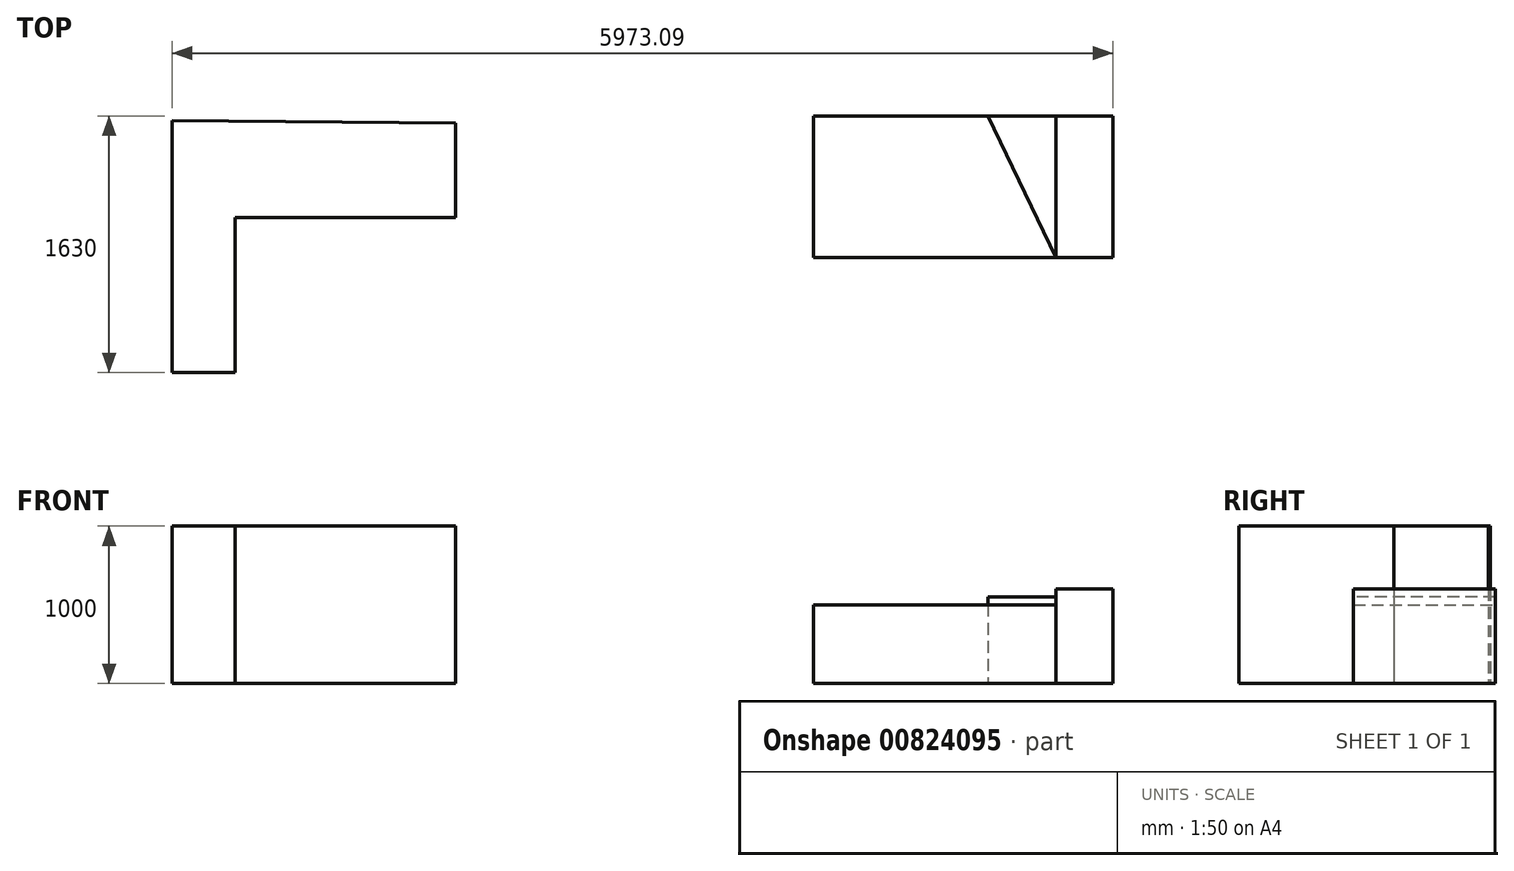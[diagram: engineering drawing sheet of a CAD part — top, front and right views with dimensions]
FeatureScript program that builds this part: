
annotation { "Feature Type Name" : "Feature", "Feature Type Description" : "" }
export const myFeature = defineFeature(function(context is Context, id is Id, definition is map)
    precondition{}
    {
        {
            var Q0;
            Q0=qCreatedBy(makeId("Top.planeOp"),FACE);
            var sketch = newSketch(context, id + "F0", { "sketchPlane" : qUnion([Q0])});
            skLineSegment(sketch, "E0.bottom", {"start": v(-91.66, 3961.41) * mm, "end": v(5908.34, 3961.41) * mm});
            skLineSegment(sketch, "E0.top", {"start": v(-91.66, -38.59) * mm, "end": v(5908.34, -38.59) * mm});
            skLineSegment(sketch, "E0.left", {"start": v(-91.66, 3961.41) * mm, "end": v(-91.66, -38.59) * mm});
            skLineSegment(sketch, "E0.right", {"start": v(5908.34, 3961.41) * mm, "end": v(5908.34, -38.59) * mm});
            skLineSegment(sketch, "E1", {"start": v(-91.66, 3926.3) * mm, "end": v(-91.66, 2326.3) * mm});
            skLineSegment(sketch, "E2", {"start": v(-91.66, 2326.3) * mm, "end": v(308.34, 2326.3) * mm});
            skLineSegment(sketch, "E3", {"start": v(308.34, 2326.3) * mm, "end": v(308.34, 3310.65) * mm});
            skLineSegment(sketch, "E4", {"start": v(308.34, 3310.65) * mm, "end": v(1708.27, 3310.65) * mm});
            skLineSegment(sketch, "E5", {"start": v(1708.27, 3910.65) * mm, "end": v(1708.27, 3310.65) * mm});
            skLineSegment(sketch, "E6", {"start": v(-91.66, 3926.3) * mm, "end": v(1708.27, 3910.65) * mm});
            skLineSegment(sketch, "E7.bottom", {"start": v(3981.43, 3056.3) * mm, "end": v(5881.43, 3056.3) * mm});
            skLineSegment(sketch, "E7.top", {"start": v(3981.43, 3956.3) * mm, "end": v(5881.43, 3956.3) * mm});
            skLineSegment(sketch, "E7.left", {"start": v(3981.43, 3056.3) * mm, "end": v(3981.43, 3956.3) * mm});
            skLineSegment(sketch, "E7.right", {"start": v(5881.43, 3056.3) * mm, "end": v(5881.43, 3956.3) * mm});
            skLineSegment(sketch, "E8.bottom", {"start": v(5881.43, 3956.3) * mm, "end": v(5521.97, 3956.3) * mm});
            skLineSegment(sketch, "E8.top", {"start": v(5881.43, 3056.3) * mm, "end": v(5521.97, 3056.3) * mm});
            skLineSegment(sketch, "E8.left", {"start": v(5881.43, 3956.3) * mm, "end": v(5881.43, 3056.3) * mm});
            skLineSegment(sketch, "E8.right", {"start": v(5521.97, 3956.3) * mm, "end": v(5521.97, 3056.3) * mm});
            skLineSegment(sketch, "E9", {"start": v(5088.45, 3956.3) * mm, "end": v(5521.97, 3056.3) * mm});
            skSolve(sketch);
        }
        {
            var Q0;
            {var subQ0=sQuery(id+"F0.wireOp",EDGE,"E2");Q0=makeQuery(id+"F0.imprint","IMPRINT",FACE,{"disambiguationData":[TD([[makeQuery(id+"F0.imprint","IMPRINT",EDGE,{"derivedFrom":subQ0}),1.0]])]});}
            extrude(context, id + "F1", {"entities" : qUnion([Q0]), "depth" : 1000 * mm, "offsetDistance" : 25 * mm});
        }
        {
            var Q0;
            {var subQ0=sQuery(id+"F0.wireOp",EDGE,"E7.left");Q0=makeQuery(id+"F0.imprint","IMPRINT",FACE,{"disambiguationData":[TD([[makeQuery(id+"F0.imprint","IMPRINT",EDGE,{"derivedFrom":subQ0}),-1.0]])]});}
            extrude(context, id + "F2", {"entities" : qUnion([Q0]), "depth" : 500 * mm, "offsetDistance" : 25 * mm});
        }
        {
            var Q0;
            {var subQ0=sQuery(id+"F0.wireOp",EDGE,"E7.right");Q0=makeQuery(id+"F0.imprint","IMPRINT",FACE,{"disambiguationData":[TD([[makeQuery(id+"F0.imprint","IMPRINT",EDGE,{"derivedFrom":subQ0}),1.0]])]});}
            extrude(context, id + "F3", {"entities" : qUnion([Q0]), "depth" : 600 * mm, "offsetDistance" : 25 * mm});
        }
        {
            var Q0;
            {var subQ0=sQuery(id+"F0.wireOp",EDGE,"E8.right");Q0=makeQuery(id+"F0.imprint","IMPRINT",FACE,{"disambiguationData":[TD([[makeQuery(id+"F0.imprint","IMPRINT",EDGE,{"derivedFrom":subQ0}),-1.0]])]});}
            extrude(context, id + "F4", {"entities" : qUnion([Q0]), "depth" : 550 * mm, "offsetDistance" : 25 * mm});
        }
    });
